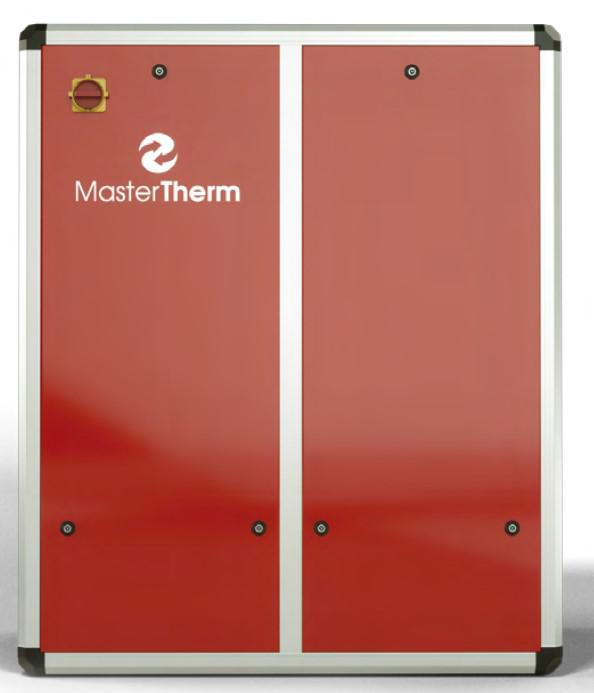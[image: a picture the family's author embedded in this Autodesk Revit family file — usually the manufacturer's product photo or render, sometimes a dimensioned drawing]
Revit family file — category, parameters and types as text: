
# Revit family: BoxAir-Inverter-P_RFA-2022_v2
name_source: partatom
category: Mechanické zařízení
units: mm (PartAtom-declared; Revit-internal decimal feet)

## family parameters
Bod výpočtu místnosti = Ne
Kóta kulaté spojky = Použít průměr
Nadpis OmniClass = Climate Control (HVAC)
Ořezat dutým tvarem při načtení = Ne
Sdílené = Ne
Typ dílu = Normální
Vždy vertikální = Ano
Zachovat orientaci poznámky = Ne
Založené na pracovní rovině = Ne
Číslo OmniClass = 23.75.00.00

## types (4) — shared parameters
Elektropřipojení = 1xPG21; 1xPG29
Kondenzát = Ø40 mm
MT_CI diameter = 28 mm  [stored 0.0918635 ft]
MT_CO diameter = 28 mm  [stored 0.0918635 ft]
MT_active power = 0 W
MT_angle offset = 60 mm  [stored 0.19685 ft]
MT_apparent power = 0 VA
MT_case mat = MT_RAL7016
MT_clearance back = 250 mm  [stored 0.82021 ft]
MT_clearance top = 200 mm  [stored 0.656168 ft]
MT_drain diameter = 40 mm  [stored 0.131234 ft]
MT_frekvence (Hz) = 50 Hz
MT_ground height = 30 mm  [stored 0.0984252 ft]
MT_pipe mat = MT_angle-corner
Otopná voda – vstup = 1'' (vnější)
Otopná voda – výstup = 1'' (vnější)
Popis = Tepelné čerpadlo vzduch/voda (R290)
URL = https://mastertherm.cz
Výrobce = Master Therm
zero-valued in all types: Cena, MT_CosPhi, Výchozí výška

## per-type parameters (varying)
- BA22IP: Komentáře k typům=KOMPRESOR: BLDC Inverter; 25 – 120 rps; olej (PZ68S) – 0.3 l; max. prov. proud – 8 A; VÝPARNÍK: lamelový (Al/Cu); přestupná plocha – 21 m2; rozteč lamel – 2.0 mm; max. přetlak – 4.2 MPa; max. průtok vzduchu – 3000 m3/h; max. příkon ventilátoru – 0.1 kW; průměr vetnilátoru – 450 mm; ot. (max) – 700 1/min; LWA – 50 dB; odtávání – reverzací; KONDENZÁTOR: deskový (nerez.); AISI316; průtok otopné vody – 0.20 kg/s; min. průtok – 0.10 kg/s; teplotní rozdíl – 5 K; objem vody – 7.0 l; max. přetlak vody – 250 kPa; max. přetlak chladiva – 4.2 MPa; ext. tlak čerpadla – 6.0 m; max. příkon čerpadla – 70 W; CHL. OKRUH: R290 (0.8 kg); ochrana úniku R290 – 35% Propylenglykol; detektor úniku – ano; EK: 5.7 + (2.8) kW; REGULACE: regulátor – pCO5; EEV – ano; čidlo otopné vody – ano; čidlo TUV – ano; ext. čidlo – ano; ekviterm. reg. – ano; chladivo – 2xPT; ESI: 1x230 (3x400) V; 50 Hz; max. proud kompresoru (EK) – 16/(16)/(16) A; el. krytí – IP43; ; ROZMĚRY: otopná voda – 1" (vnější); 90x130x53 cm; 120 kg; LIMITNÍ PROVOZNÍ PARAMETRY: max. přetlak vody – 0.25 MPa; max. přetlak chladiva – 2.9 MPa; vzduch min./max.: -20/+35 °C; voda min./max.: 20/65 °C; MT_TYPE=22; MT_angle length_X=1184 mm  [stored 3.88451 ft]; MT_angle length_Y=406 mm  [stored 1.33202 ft]; MT_angle length_Z=765 mm  [stored 2.50984 ft]; MT_case depth=526 mm  [stored 1.72572 ft]; MT_case height=885 mm  [stored 2.90354 ft]; MT_case width=1304 mm  [stored 4.27822 ft]; MT_clearance front=1500 mm  [stored 4.92126 ft]; MT_clearance left=1500 mm  [stored 4.92126 ft]; MT_clearance right=1500 mm  [stored 4.92126 ft]; MT_cover front_X=1224 mm  [stored 4.01575 ft]; MT_cover front_Y=805 mm  [stored 2.64108 ft]; MT_cover front_Y-v2=-526 mm  [stored -1.72572 ft]; MT_cover side_X=446 mm  [stored 1.46325 ft]; MT_cover side_Y=805 mm  [stored 2.64108 ft]; MT_cover top_X=1224 mm  [stored 4.01575 ft]; MT_cover top_Y=446 mm  [stored 1.46325 ft]; MT_front grille H=805 mm  [stored 2.64108 ft]; MT_front grille W=726 mm  [stored 2.38189 ft]; MT_grille ext front Y=755 mm  [stored 2.47703 ft]; MT_hmotnost (kg)=120; MT_max. proud – elektrokotel (A)=16 A; MT_max. proud – kompresor (A)=16 A; MT_napětí (V)=230 V; MT_side grille H=805 mm  [stored 2.64108 ft]; MT_side grille W=446 mm  [stored 1.46325 ft]; Model=BoxAir 22 Intverter P
- BA26IP: Komentáře k typům=KOMPRESOR: BLDC Inverter; 15 – 110 rps; olej (PZ68S) – 0.75 l; max. prov. proud – 21 A; VÝPARNÍK: lamelový (Al/Cu); přestupná plocha – 21 m2; rozteč lamel – 2.0 mm; max. přetlak – 4.2 MPa; max. průtok vzduchu – 3500 m3/h; max. příkon ventilátoru – 0.1 kW; průměr vetnilátoru – 450 mm; ot. (max) – 700 1/min; LWA – 53 dB; odtávání – reverzací; KONDENZÁTOR: deskový (nerez.); AISI316; průtok otopné vody – 0.27 kg/s; min. průtok – 0.13 kg/s; teplotní rozdíl – 5 K; objem vody – 7.0 l; max. přetlak vody – 250 kPa; max. přetlak chladiva – 4.2 MPa; ext. tlak čerpadla – 6.0 m; max. příkon čerpadla – 70 W; CHL. OKRUH: R290 (0.9 kg); ochrana úniku R290 – 35% Propylenglykol; detektor úniku – ano; EK: 5.7 + (2.8) kW; REGULACE: regulátor – pCO5; EEV – ano; čidlo otopné vody – ano; čidlo TUV – ano; ext. čidlo – ano; ekviterm. reg. – ano; chladivo – 2xPT; ESI: 1x230 (3x400) V; 50 Hz; max. proud kompresoru (EK) – 20/(16)/(16) A; el. krytí – IP43; ; ROZMĚRY: otopná voda – 1" (vnější); 90x130x53 cm; 130 kg; LIMITNÍ PROVOZNÍ PARAMETRY: max. přetlak vody – 0.25 MPa; max. přetlak chladiva – 2.9 MPa; vzduch min./max.: -20/+35 °C; voda min./max.: 20/65 °C; MT_TYPE=26; MT_angle length_X=1184 mm  [stored 3.88451 ft]; MT_angle length_Y=406 mm  [stored 1.33202 ft]; MT_angle length_Z=765 mm  [stored 2.50984 ft]; MT_case depth=526 mm  [stored 1.72572 ft]; MT_case height=885 mm  [stored 2.90354 ft]; MT_case width=1304 mm  [stored 4.27822 ft]; MT_clearance front=1500 mm  [stored 4.92126 ft]; MT_clearance left=1500 mm  [stored 4.92126 ft]; MT_clearance right=1500 mm  [stored 4.92126 ft]; MT_cover front_X=1224 mm  [stored 4.01575 ft]; MT_cover front_Y=805 mm  [stored 2.64108 ft]; MT_cover front_Y-v2=-526 mm  [stored -1.72572 ft]; MT_cover side_X=446 mm  [stored 1.46325 ft]; MT_cover side_Y=805 mm  [stored 2.64108 ft]; MT_cover top_X=1224 mm  [stored 4.01575 ft]; MT_cover top_Y=446 mm  [stored 1.46325 ft]; MT_front grille H=805 mm  [stored 2.64108 ft]; MT_front grille W=726 mm  [stored 2.38189 ft]; MT_grille ext front Y=755 mm  [stored 2.47703 ft]; MT_hmotnost (kg)=130; MT_max. proud – elektrokotel (A)=16 A; MT_max. proud – kompresor (A)=20 A; MT_napětí (V)=230 V; MT_side grille H=805 mm  [stored 2.64108 ft]; MT_side grille W=446 mm  [stored 1.46325 ft]; Model=BoxAir 26 Intverter P
- BA37IP: Komentáře k typům=KOMPRESOR: BLDC Inverter; 15 – 100 rps; olej (PZ68S) – 0.9 l; max. prov. proud – 21 A; VÝPARNÍK: lamelový (Al/Cu); přestupná plocha – 42 m2; rozteč lamel – 2.0 mm; max. přetlak – 3.0 MPa; max. průtok vzduchu – 8000 m3/h; max. příkon ventilátoru – 0.2 kW; průměr vetnilátoru – 2x450 mm; ot. (max) – 700 1/min; LWA – 55 dB; odtávání – reverzací; KONDENZÁTOR: deskový (nerez.); AISI316; průtok otopné vody – 0.46 kg/s; min. průtok – 0.23 kg/s; teplotní rozdíl – 5 K; objem vody – 10.9 l; max. přetlak vody – 250 kPa; max. přetlak chladiva – 3.0 MPa; ext. tlak čerpadla – 6.0 m; max. příkon čerpadla – 130 W; CHL. OKRUH: R290 (1.55 kg); ochrana úniku R290 – 35% Propylenglykol; detektor úniku – ano; EK: 7.5 + (7.5) kW; REGULACE: regulátor – pCO5; EEV – ano; čidlo otopné vody – ano; čidlo TUV – ano; ext. čidlo – ano; ekviterm. reg. – ano; chladivo – 2xPT; ESI: 3x400 V; 50 Hz; max. proud kompresoru (EK) – 20 (25) A; el. krytí – IP44; ; ROZMĚRY: otopná voda – 1" (vnější); 150x130x53 cm; 165 kg; LIMITNÍ PROVOZNÍ PARAMETRY: max. přetlak vody – 0.25 MPa; max. přetlak chladiva – 2.9 MPa; vzduch min./max.: -20/+35 °C; voda min./max.: 20/65 °C; MT_TYPE=37; MT_angle length_X=1188 mm; MT_angle length_Y=408 mm; MT_angle length_Z=1378 mm  [stored 4.521 ft]; MT_case depth=528 mm  [stored 1.73228 ft]; MT_case height=1498 mm  [stored 4.9147 ft]; MT_case width=1308 mm; MT_clearance front=2000 mm  [stored 6.56168 ft]; MT_clearance left=2000 mm  [stored 6.56168 ft]; MT_clearance right=2000 mm  [stored 6.56168 ft]; MT_cover front_X=1228 mm; MT_cover front_Y=1418 mm  [stored 4.65223 ft]; MT_cover front_Y-v2=-528 mm  [stored -1.73228 ft]; MT_cover side_X=448 mm  [stored 1.46982 ft]; MT_cover side_Y=1418 mm  [stored 4.65223 ft]; MT_cover top_X=1228 mm; MT_cover top_Y=448 mm  [stored 1.46982 ft]; MT_front grille H=1418 mm  [stored 4.65223 ft]; MT_front grille W=730 mm; MT_grille ext front Y=1368 mm  [stored 4.48819 ft]; MT_hmotnost (kg)=165; MT_max. proud – elektrokotel (A)=25 A; MT_max. proud – kompresor (A)=20 A; MT_napětí (V)=400 V; MT_side grille H=1418 mm  [stored 4.65223 ft]; MT_side grille W=448 mm  [stored 1.46982 ft]; Model=BoxAir 37 Intverter P
- BA45IP: Komentáře k typům=KOMPRESOR: BLDC Inverter; 15 – 90 rps; olej (HAF68D1U) – 2.0 l; max. prov. proud – 24 A; VÝPARNÍK: lamelový (Al/Cu); přestupná plocha – 42 m2; rozteč lamel – 2.0 mm; max. přetlak – 3.0 MPa; max. průtok vzduchu – 8000 m3/h; max. příkon ventilátoru – 0.2 kW; průměr vetnilátoru – 2x450 mm; ot. (max) – 700 1/min; LWA – 60 dB; odtávání – reverzací; KONDENZÁTOR: deskový (nerez.); AISI316; průtok otopné vody – 0.55 kg/s; min. průtok – 0.27 kg/s; teplotní rozdíl – 5 K; objem vody – 10.9 l; max. přetlak vody – 250 kPa; max. přetlak chladiva – 3.0 MPa; ext. tlak čerpadla – 6.0 m; max. příkon čerpadla – 130 W; CHL. OKRUH: R290 (1.55 kg); ochrana úniku R290 – 35% Propylenglykol; detektor úniku – ano; EK: 7.5 + (7.5) kW; REGULACE: regulátor – pCO5; EEV – ano; čidlo otopné vody – ano; čidlo TUV – ano; ext. čidlo – ano; ekviterm. reg. – ano; chladivo – 2xPT; ESI: 3x400 V; 50 Hz; max. proud kompresoru (EK) – 25 (32) A; el. krytí – IP43; ; ROZMĚRY: otopná voda – 1" (vnější); 150x130x53 cm; 185 kg; LIMITNÍ PROVOZNÍ PARAMETRY: max. přetlak vody – 0.25 MPa; max. přetlak chladiva – 2.9 MPa; vzduch min./max.: -20/+35 °C; voda min./max.: 20/65 °C; MT_TYPE=45; MT_angle length_X=1188 mm; MT_angle length_Y=408 mm; MT_angle length_Z=1378 mm  [stored 4.521 ft]; MT_case depth=528 mm  [stored 1.73228 ft]; MT_case height=1498 mm  [stored 4.9147 ft]; MT_case width=1308 mm; MT_clearance front=2000 mm  [stored 6.56168 ft]; MT_clearance left=2000 mm  [stored 6.56168 ft]; MT_clearance right=2000 mm  [stored 6.56168 ft]; MT_cover front_X=1228 mm; MT_cover front_Y=1418 mm  [stored 4.65223 ft]; MT_cover front_Y-v2=-528 mm  [stored -1.73228 ft]; MT_cover side_X=448 mm  [stored 1.46982 ft]; MT_cover side_Y=1418 mm  [stored 4.65223 ft]; MT_cover top_X=1228 mm; MT_cover top_Y=448 mm  [stored 1.46982 ft]; MT_front grille H=1418 mm  [stored 4.65223 ft]; MT_front grille W=730 mm; MT_grille ext front Y=1368 mm  [stored 4.48819 ft]; MT_hmotnost (kg)=185; MT_max. proud – elektrokotel (A)=32 A; MT_max. proud – kompresor (A)=25 A; MT_napětí (V)=400 V; MT_side grille H=1418 mm  [stored 4.65223 ft]; MT_side grille W=448 mm  [stored 1.46982 ft]; Model=BoxAir 45 Intverter P

note: [stored X ft] marks values corroborated as IEEE doubles in the binary element streams (Revit-internal decimal feet)
